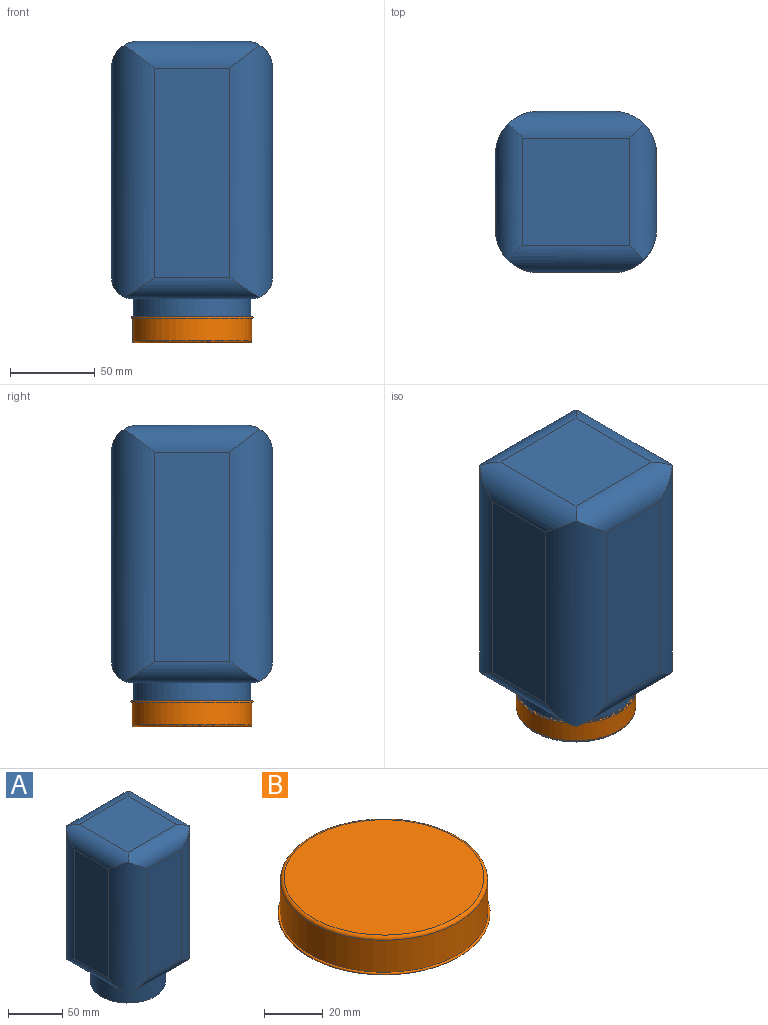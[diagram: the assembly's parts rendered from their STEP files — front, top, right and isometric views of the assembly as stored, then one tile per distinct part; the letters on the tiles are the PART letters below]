
ASSEMBLY  parts=2 mates=1
PART A: 39 faces, bbox 95.3x95.3x177.8 mm
  f0: cylinder r=25.4mm len=148.83mm, axis (0,0,-1), area 5487.8mm2, adj f6,f8,f9,f12,f16,f19
  f1: cylinder r=25.4mm len=148.83mm, axis (0,0,-1), area 5487.8mm2, adj f6,f10,f11,f13,f16,f19
  f2: cylinder r=25.4mm len=148.83mm, axis (0,0,-1), area 5487.8mm2, adj f7,f10,f11,f13,f17,f18
  f3: cylinder r=25.4mm len=148.83mm, axis (0,0,-1), area 5487.8mm2, adj f7,f8,f9,f12,f17,f18
  f4: plane 63.5x63.5mm, normal (0,0,1), area 4032.3mm2, adj f9,f10,f18,f19
  f5: plane 69.85x69.85mm, normal (0,0,-1), area 1086mm2, adj f8,f11,f14,f16,f17
  f6: plane 123.83x44.45mm, normal (0,1,0), area 5504mm2, adj f0,f1,f16,f19
  f7: plane 123.83x44.45mm, normal (0,-1,0), area 5504mm2, adj f2,f3,f17,f18
  f8: cylinder r=12.7mm len=80.37mm, axis (0,-1,0), area 1332.1mm2, adj f0,f3,f5,f12,f16,f17
  f9: cylinder r=15.88mm len=80.37mm, axis (0,-1,0), area 1661.3mm2, adj f0,f3,f4,f12,f18,f19
  f10: cylinder r=15.88mm len=80.37mm, axis (0,-1,0), area 1661.3mm2, adj f1,f2,f4,f13,f18,f19
  f11: cylinder r=12.7mm len=80.37mm, axis (0,-1,0), area 1332.1mm2, adj f1,f2,f5,f13,f16,f17
  f12: plane 123.83x44.45mm, normal (1,0,0), area 5504mm2, adj f0,f3,f8,f9
  f13: plane 123.83x44.45mm, normal (-1,0,0), area 5504mm2, adj f1,f2,f10,f11
  f14: cylinder r=34.75mm len=69.49mm, axis (0,0,-1), area 5545.4mm2, adj f5,f15
  f15: plane 69.49x69.49mm, normal (0,0,-1), area 636.3mm2, adj f14,f34
  f16: cylinder r=12.7mm len=80.37mm, axis (1,0,0), area 1332.1mm2, adj f0,f1,f5,f6,f8,f11
  f17: cylinder r=12.7mm len=80.37mm, axis (1,0,0), area 1332.1mm2, adj f2,f3,f5,f7,f8,f11
  f18: cylinder r=15.88mm len=80.37mm, axis (1,0,0), area 1661.3mm2, adj f2,f3,f4,f7,f9,f10
  f19: cylinder r=15.88mm len=80.37mm, axis (1,0,0), area 1661.3mm2, adj f0,f1,f4,f6,f9,f10
  f20: cylinder r=22.35mm len=144.15mm, axis (0,0,-1), area 4744mm2, adj f26,f28,f29,f32,f35,f38
  f21: cylinder r=22.35mm len=144.15mm, axis (0,0,-1), area 4744mm2, adj f26,f30,f31,f33,f35,f38
  f22: cylinder r=22.35mm len=144.15mm, axis (0,0,-1), area 4744mm2, adj f27,f30,f31,f33,f36,f37
  f23: cylinder r=22.35mm len=144.15mm, axis (0,0,-1), area 4744mm2, adj f27,f28,f29,f32,f36,f37
  f24: plane 63.5x63.5mm, normal (0,0,-1), area 4032.3mm2, adj f29,f30,f37,f38
  f25: plane 69.85x69.85mm, normal (0,0,1), area 1722.2mm2, adj f28,f31,f34,f35,f36
  f26: plane 123.83x44.45mm, normal (0,-1,0), area 5504mm2, adj f20,f21,f35,f38
  f27: plane 123.83x44.45mm, normal (0,1,0), area 5504mm2, adj f22,f23,f36,f37
  f28: cylinder r=9.65mm len=76.06mm, axis (0,-1,0), area 968mm2, adj f20,f23,f25,f32,f35,f36
  f29: cylinder r=12.83mm len=76.06mm, axis (0,-1,0), area 1291.6mm2, adj f20,f23,f24,f32,f37,f38
  f30: cylinder r=12.83mm len=76.06mm, axis (0,-1,0), area 1291.6mm2, adj f21,f22,f24,f33,f37,f38
  f31: cylinder r=9.65mm len=76.06mm, axis (0,-1,0), area 968mm2, adj f21,f22,f25,f33,f35,f36
  f32: plane 123.83x44.45mm, normal (-1,0,0), area 5504mm2, adj f20,f23,f28,f29
  f33: plane 123.83x44.45mm, normal (1,0,0), area 5504mm2, adj f21,f22,f30,f31
  f34: cylinder r=31.7mm len=63.4mm, axis (0,0,-1), area 5666mm2, adj f15,f25
  f35: cylinder r=9.65mm len=76.06mm, axis (1,0,0), area 968mm2, adj f20,f21,f25,f26,f28,f31
  f36: cylinder r=9.65mm len=76.06mm, axis (1,0,0), area 968mm2, adj f22,f23,f25,f27,f28,f31
  f37: cylinder r=12.83mm len=76.06mm, axis (1,0,0), area 1291.6mm2, adj f22,f23,f24,f27,f29,f30
  f38: cylinder r=12.83mm len=76.06mm, axis (1,0,0), area 1291.6mm2, adj f20,f21,f24,f26,f29,f30
PART B: 8 faces, bbox 78.1x78.1x15.3 mm
  f0: plane 71.35x71.35mm, normal (0,0,-1), area 202.3mm2, adj f1,f7
  f1: torus R=35.67mm, axis (0,0,1), area 430.3mm2, adj f0,f2
  f2: cylinder r=35.27mm len=70.54mm, axis (0,0,1), area 3022.5mm2, adj f1,f3
  f3: torus R=34mm, axis (0,0,1), area 436.3mm2, adj f2,f4
  f4: plane 68x68mm, normal (0,0,1), area 3631.2mm2, adj f3
  f5: plane 68x68mm, normal (0,0,-1), area 3631.2mm2, adj f6
  f6: torus R=34mm, axis (0,0,1), area 259.3mm2, adj f5,f7
  f7: cylinder r=34.76mm len=69.52mm, axis (0,0,1), area 3067.7mm2, adj f0,f6
PLACE A at identity
PLACE B rot(axis=(1,0,0),180deg) t=(0,0,-25.91)mm
MATE planar B.f1 <-> A.f14  axis (0,0,1) through (0,0,-25.4)mm
